# Revit family: GALAD Икар LED
name_source: partatom
category: Осветительные приборы
revit_build: Autodesk Revit 2018 (Build: 20180423_1000(x64)
units: mm (PartAtom-declared; Revit-internal decimal feet)

## family parameters
Источник света = Да
Общий = Нет
Основа = Грань
При загрузке вырезать с полостями = Нет
Размер круглого соединителя = Использовать диаметр
Тип детали = Нормальный
Точка расчета площади = Нет

## types (1)
- GALAD Икар LED
    ADSK_Версия Revit = 2018
    ADSK_Версия семейства = 1.01
    ADSK_Единица измерения = шт.
    ADSK_Завод-изготовитель = Лихославльский завод Светотехника
    ADSK_Классификация нагрузок = Освещение
    ADSK_Код изделия = 13840
    ADSK_Количество = 1
    ADSK_Количество фаз = 1
    ADSK_Коэффициент мощности = 0.96
    ADSK_Марка = GALAD Икар LED-40-СПШ/Т60 (3700/750/RAL7040/D/0/GEN1)
    ADSK_Масса = 2.7
    ADSK_Масса_Текст = 2.7
    ADSK_Наименование = GALAD Икар LED-40-СПШ/Т60 (3700/750/RAL7040/D/0/GEN1)
    ADSK_Наименование краткое = GALAD Икар LED-40
    ADSK_Напряжение = 230 В
    ADSK_Номинальная мощность = 40 Вт
    ADSK_Обозначение = ГОСТ 54350, ГОСТ 12.2.007.0, ГОСТ 17516.1, ГОСТ 15150
    ADSK_Полная мощность = 42 В·А
    ADSK_Размер_Высота = 424 мм
    ADSK_Размер_Длина = 316 мм
    ADSK_Размер_Ширина = 316 мм
    ADSK_Ток = 0 А
    ADSK_Энергоэффективность = 93 лм/Вт
    IP = 54
    URL = https://galad.ru
    Блок аварийного питания = Нет
    Возможный угол наклона = 0
    Группа модели = Светильники
    Диапазон цветовой температуры = 5028±283
    Изготовитель = Лихославльский завод Светотехника
    Класс Защиты = 1
    Класс защиты от поражения электрическим током = 1
    Класс светораспределения = Р
    Климатическая зона = У1
    Климатическое исполнение = -40…40 °С
    Код по ETIM = 0
    Коэффициент пульсации = менее 10%
    Область использования = Садово-парковое освещение
    Описание = Классическая, привычная всем, форма светильника в современном светодиодном исполнении. Такие светильники освещают парки, скверы, бульвары, а иногда даже и улицы каждого российского города. Цельнолитое основание обеспечивает оптимальный теплоотвод, а антивандальный рассеиватель из ударопрочного светостабилизированного поликарбоната лучше сохраняет свой внешний вид и оптические свойства, по сравнению с обычным поликарбонатом.
    Отметка по умолчанию = 0 мм
    Полная установленная мощность = 42 В·А
    Световая отдача = 93
    Светофильтр = 16777215
    Смещение цветовой температуры при затухании лампы = <Нет>
    Снижение светового потока во время разгорания = не более 6%
    Срок службы = 12 лет
    Тип КСС = 0
    Тип ПРА = ЭПРА
    Тип источника света = LED
    Тип монтажной поверхности = Торшер
    Тип продукции = Светильник
    Тип устройства управления светодиодами = Без управления
    Угол наклона = 90.00°
    Файл фотометрической сетки = GALAD Ikar (3700-750-RAL7040-D-0-GEN1).ies
    Цветопередача = 80
    Частота = 50
